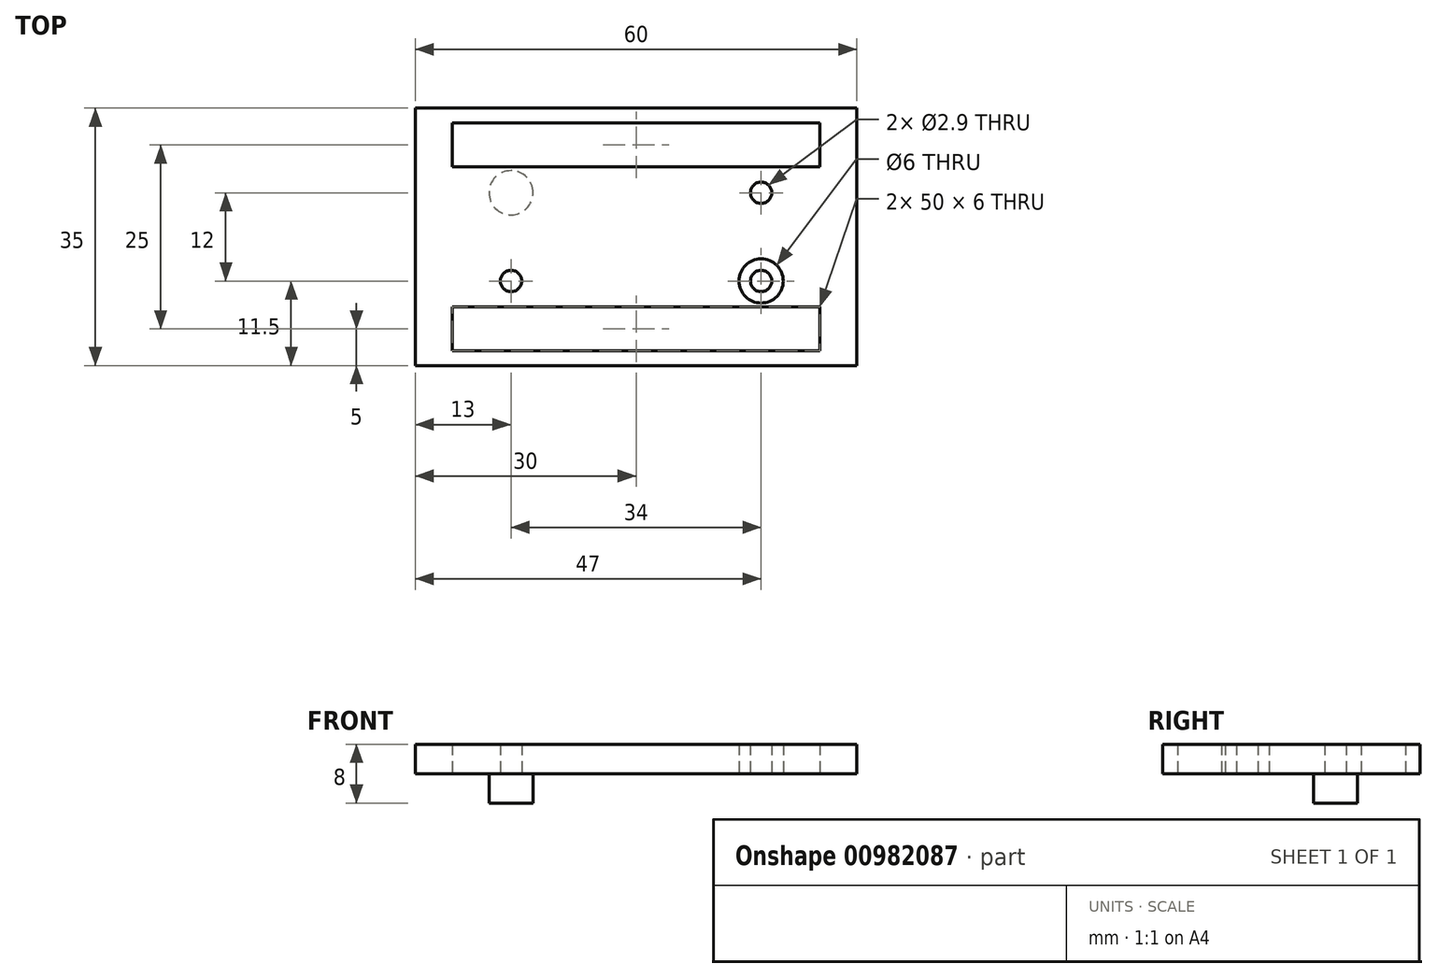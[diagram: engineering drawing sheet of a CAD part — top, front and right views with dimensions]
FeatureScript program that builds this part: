
annotation { "Feature Type Name" : "Feature", "Feature Type Description" : "" }
export const myFeature = defineFeature(function(context is Context, id is Id, definition is map)
    precondition{}
    {
        {
            var Q0;
            Q0=qCreatedBy(makeId("Top.planeOp"),FACE);
            var sketch = newSketch(context, id + "F0", { "sketchPlane" : qUnion([Q0])});
            skLineSegment(sketch, "E0.bottom", {"start": v(-30, 17.5) * mm, "end": v(30, 17.5) * mm});
            skLineSegment(sketch, "E0.top", {"start": v(-30, -17.5) * mm, "end": v(30, -17.5) * mm});
            skLineSegment(sketch, "E0.left", {"start": v(-30, 17.5) * mm, "end": v(-30, -17.5) * mm});
            skLineSegment(sketch, "E0.right", {"start": v(30, 17.5) * mm, "end": v(30, -17.5) * mm});
            skPoint(sketch, "E0.middle", {"position": v(0, 0) * mm});
            skLineSegment(sketch, "E1", {"start": v(-30, 17.5) * mm, "end": v(-30, 12.5) * mm, "construction": true});
            skLineSegment(sketch, "E2", {"start": v(-30, 12.5) * mm, "end": v(-25, 12.5) * mm, "construction": true});
            skLineSegment(sketch, "E3", {"start": v(30, 17.5) * mm, "end": v(30, 12.5) * mm, "construction": true});
            skLineSegment(sketch, "E4", {"start": v(30, 12.5) * mm, "end": v(25, 12.5) * mm, "construction": true});
            skLineSegment(sketch, "E5.bottom", {"start": v(-25, 12.5) * mm, "end": v(25, 12.5) * mm});
            skLineSegment(sketch, "E5.top", {"start": v(-25, 15.5) * mm, "end": v(25, 15.5) * mm});
            skLineSegment(sketch, "E5.left", {"start": v(-25, 12.5) * mm, "end": v(-25, 15.5) * mm});
            skLineSegment(sketch, "E5.right", {"start": v(25, 12.5) * mm, "end": v(25, 15.5) * mm});
            skLineSegment(sketch, "E6.MirrorCS", {"start": v(-25, 9.5) * mm, "end": v(25, 9.5) * mm});
            skLineSegment(sketch, "E7.MirrorCS", {"start": v(-25, 12.5) * mm, "end": v(-25, 9.5) * mm});
            skLineSegment(sketch, "E8.MirrorCS", {"start": v(25, 12.5) * mm, "end": v(25, 9.5) * mm});
            skLineSegment(sketch, "E9.MirrorCS", {"start": v(-25, -9.5) * mm, "end": v(25, -9.5) * mm});
            skLineSegment(sketch, "E10.MirrorCS", {"start": v(-25, -15.5) * mm, "end": v(25, -15.5) * mm});
            skLineSegment(sketch, "E11.MirrorCS", {"start": v(-25, -12.5) * mm, "end": v(-25, -15.5) * mm});
            skLineSegment(sketch, "E12.MirrorCS", {"start": v(-25, -12.5) * mm, "end": v(-25, -9.5) * mm});
            skLineSegment(sketch, "E13.MirrorCS", {"start": v(25, -12.5) * mm, "end": v(25, -9.5) * mm});
            skLineSegment(sketch, "E14.MirrorCS", {"start": v(25, -12.5) * mm, "end": v(25, -15.5) * mm});
            skLineSegment(sketch, "E15.bottom", {"start": v(25, 12.5) * mm, "end": v(-25, 12.5) * mm});
            skLineSegment(sketch, "E15.top", {"start": v(25, 14.1) * mm, "end": v(-25, 14.1) * mm});
            skLineSegment(sketch, "E15.left", {"start": v(25, 12.5) * mm, "end": v(25, 14.1) * mm});
            skLineSegment(sketch, "E15.right", {"start": v(-25, 12.5) * mm, "end": v(-25, 14.1) * mm});
            skLineSegment(sketch, "E16.MirrorCS", {"start": v(25, 10.9) * mm, "end": v(-25, 10.9) * mm});
            skLineSegment(sketch, "E17.MirrorCS", {"start": v(25, -10.9) * mm, "end": v(-25, -10.9) * mm});
            skLineSegment(sketch, "E18.MirrorCS", {"start": v(25, -14.1) * mm, "end": v(-25, -14.1) * mm});
            skLineSegment(sketch, "E19", {"start": v(-21.28, 14.1) * mm, "end": v(-21.28, 10.9) * mm, "construction": true});
            skLineSegment(sketch, "E20", {"start": v(-7.7, -10.9) * mm, "end": v(-7.7, -14.1) * mm, "construction": true});
            skSolve(sketch);
        }
        {
            var Q0;
            Q0=makeQuery(id+"F0.imprint","IMPRINT",FACE,{"disambiguationData":[TD([[makeQuery(id+"F0.imprint","IMPRINT",EDGE,{"derivedFrom":sQuery(id+"F0.wireOp",EDGE,"E0.bottom")}),-1.0]])]});
            extrude(context, id + "F1", {"entities" : qUnion([Q0]), "depth" : 8 * mm, "offsetDistance" : 25 * mm});
        }
        {
            var Q0;
            Q0=makeQuery(id+"F0.imprint","IMPRINT",FACE,{"disambiguationData":[TD([[makeQuery(id+"F0.imprint","IMPRINT",EDGE,{"derivedFrom":sQuery(id+"F0.wireOp",EDGE,"E5.top")}),-1.0]])]});
            var Q1;
            {var subQ0=sQuery(id+"F0.wireOp",EDGE,"E6.MirrorCS");Q1=makeQuery(id+"F0.imprint","IMPRINT",FACE,{"disambiguationData":[TD([[makeQuery(id+"F0.imprint","IMPRINT",EDGE,{"derivedFrom":subQ0}),1.0]])]});}
            var Q2;
            {var subQ0=sQuery(id+"F0.wireOp",EDGE,"E9.MirrorCS");Q2=makeQuery(id+"F0.imprint","IMPRINT",FACE,{"disambiguationData":[TD([[makeQuery(id+"F0.imprint","IMPRINT",EDGE,{"derivedFrom":subQ0}),-1.0]])]});}
            var Q3;
            {var subQ0=sQuery(id+"F0.wireOp",EDGE,"E10.MirrorCS");Q3=makeQuery(id+"F0.imprint","IMPRINT",FACE,{"disambiguationData":[TD([[makeQuery(id+"F0.imprint","IMPRINT",EDGE,{"derivedFrom":subQ0}),1.0]])]});}
            extrude(context, id + "F2", {"entities" : qUnion([Q0, Q1, Q2, Q3]), "operationType" : NewBodyOperationType.ADD, "depth" : 3 * mm, "offsetDistance" : 25 * mm});
        }
        {
            var Q0;
            {var subQ0=sQuery(id+"F0.wireOp",EDGE,"E14.MirrorCS");var subQ1=sQuery(id+"F0.wireOp",EDGE,"E11.MirrorCS");var subQ2=sQuery(id+"F0.wireOp",EDGE,"E10.MirrorCS");var subQ3=sQuery(id+"F0.wireOp",EDGE,"E13.MirrorCS");var subQ4=sQuery(id+"F0.wireOp",EDGE,"E12.MirrorCS");var subQ5=sQuery(id+"F0.wireOp",EDGE,"E9.MirrorCS");var subQ6=sQuery(id+"F0.wireOp",EDGE,"E8.MirrorCS");var subQ7=sQuery(id+"F0.wireOp",EDGE,"E7.MirrorCS");var subQ8=sQuery(id+"F0.wireOp",EDGE,"E6.MirrorCS");var subQ9=sQuery(id+"F0.wireOp",EDGE,"E5.right");var subQ10=sQuery(id+"F0.wireOp",EDGE,"E5.left");var subQ11=sQuery(id+"F0.wireOp",EDGE,"E5.top");Q0=makeQuery(id+"F2.boolean.opBoolean","MERGE",FACE,{"derivedFrom":[makeQuery(id+"F1.opExtrude","CAP_FACE",FACE,{"disambiguationData":[OSD([sQuery(id+"F0.wireOp",EDGE,"E0.bottom"),sQuery(id+"F0.wireOp",EDGE,"E0.top"),sQuery(id+"F0.wireOp",EDGE,"E0.left"),sQuery(id+"F0.wireOp",EDGE,"E0.right"),subQ11,subQ10,subQ9,subQ8,subQ7,subQ6,subQ5,subQ2,subQ1,subQ4,subQ3,subQ0,sQuery(id+"F0.wireOp",EDGE,"E15.left"),sQuery(id+"F0.wireOp",EDGE,"E15.right")])],"isStart":true}),makeQuery(id+"F2.opExtrude","CAP_FACE",FACE,{"disambiguationData":[OSD([subQ11,subQ10,subQ9,sQuery(id+"F0.wireOp",EDGE,"E15.top")])],"isStart":true}),makeQuery(id+"F2.opExtrude","CAP_FACE",FACE,{"disambiguationData":[OSD([subQ8,subQ7,subQ6,sQuery(id+"F0.wireOp",EDGE,"E16.MirrorCS")])],"isStart":true}),makeQuery(id+"F2.opExtrude","CAP_FACE",FACE,{"disambiguationData":[OSD([subQ5,subQ4,subQ3,sQuery(id+"F0.wireOp",EDGE,"E17.MirrorCS")])],"isStart":true}),makeQuery(id+"F2.opExtrude","CAP_FACE",FACE,{"disambiguationData":[OSD([subQ2,subQ1,subQ0,sQuery(id+"F0.wireOp",EDGE,"E18.MirrorCS")])],"isStart":true})]});}
            var sketch = newSketch(context, id + "F3", { "sketchPlane" : qUnion([Q0])});
            skLineSegment(sketch, "E21.bottom", {"start": v(17, -6) * mm, "end": v(-17, -6) * mm});
            skLineSegment(sketch, "E21.top", {"start": v(17, 6) * mm, "end": v(-17, 6) * mm});
            skLineSegment(sketch, "E21.left", {"start": v(17, -6) * mm, "end": v(17, 6) * mm});
            skLineSegment(sketch, "E21.right", {"start": v(-17, -6) * mm, "end": v(-17, 6) * mm});
            skPoint(sketch, "E21.middle", {"position": v(0, 0) * mm});
            skCircle(sketch, "E22", {"center": v(-17, 6) * mm, "radius": 3 * mm});
            skCircle(sketch, "E23", {"center": v(-17, 6) * mm, "radius": 1.45 * mm});
            skCircle(sketch, "E24.MirrorC", {"center": v(17, 6) * mm, "radius": 1.45 * mm});
            skCircle(sketch, "E25.MirrorC", {"center": v(17, 6) * mm, "radius": 3 * mm});
            skCircle(sketch, "E26.MirrorC", {"center": v(-17, -6) * mm, "radius": 3 * mm});
            skCircle(sketch, "E27.MirrorC", {"center": v(-17, -6) * mm, "radius": 1.45 * mm});
            skCircle(sketch, "E28.MirrorC", {"center": v(17, -6) * mm, "radius": 3 * mm});
            skCircle(sketch, "E29.MirrorC", {"center": v(17, -6) * mm, "radius": 1.45 * mm});
            skLineSegment(sketch, "E30.MirrorCS", {"start": v(-17, 6) * mm, "end": v(-17, -6) * mm});
            skLineSegment(sketch, "E31.MirrorCS", {"start": v(17, 6) * mm, "end": v(17, -6) * mm});
            skSolve(sketch);
        }
        {
            var Q0;
            {var subQ0=sQuery(id+"F3.wireOp",EDGE,"E30.MirrorCS");var subQ1=sQuery(id+"F3.wireOp",EDGE,"E22");var subQ2=makeQuery(id+"F3.imprint","INTERSECT",VERTEX,{"derivedFrom":[subQ1,subQ0]});Q0=makeQuery(id+"F3.imprint","IMPRINT",FACE,{"disambiguationData":[TD([[makeQuery(id+"F3.imprint","IMPRINT",EDGE,{"disambiguationData":[TD([[subQ2,1.0]])],"derivedFrom":subQ1}),1.0]])]});}
            var Q1;
            {var subQ0=sQuery(id+"F3.wireOp",EDGE,"E30.MirrorCS");var subQ1=sQuery(id+"F3.wireOp",EDGE,"E22");var subQ2=makeQuery(id+"F3.imprint","INTERSECT",VERTEX,{"derivedFrom":[subQ1,subQ0]});Q1=makeQuery(id+"F3.imprint","IMPRINT",FACE,{"disambiguationData":[TD([[makeQuery(id+"F3.imprint","IMPRINT",EDGE,{"disambiguationData":[TD([[subQ2,-1.0]])],"derivedFrom":subQ1}),1.0]])]});}
            var Q2;
            {var subQ0=sQuery(id+"F3.wireOp",EDGE,"E21.bottom");var subQ1=sQuery(id+"F3.wireOp",EDGE,"E26.MirrorC");var subQ2=makeQuery(id+"F3.imprint","INTERSECT",VERTEX,{"derivedFrom":[subQ1,subQ0]});Q2=makeQuery(id+"F3.imprint","IMPRINT",FACE,{"disambiguationData":[TD([[makeQuery(id+"F3.imprint","IMPRINT",EDGE,{"disambiguationData":[TD([[subQ2,-1.0]])],"derivedFrom":subQ1}),-1.0]])]});}
            var Q3;
            {var subQ0=sQuery(id+"F3.wireOp",EDGE,"E21.bottom");var subQ1=sQuery(id+"F3.wireOp",EDGE,"E26.MirrorC");var subQ2=makeQuery(id+"F3.imprint","INTERSECT",VERTEX,{"derivedFrom":[subQ1,subQ0]});Q3=makeQuery(id+"F3.imprint","IMPRINT",FACE,{"disambiguationData":[TD([[makeQuery(id+"F3.imprint","IMPRINT",EDGE,{"disambiguationData":[TD([[subQ2,1.0]])],"derivedFrom":subQ1}),-1.0]])]});}
            var Q4;
            {var subQ0=sQuery(id+"F3.wireOp",EDGE,"E21.top");var subQ1=sQuery(id+"F3.wireOp",EDGE,"E24.MirrorC");var subQ2=makeQuery(id+"F3.imprint","INTERSECT",VERTEX,{"derivedFrom":[subQ1,subQ0]});Q4=makeQuery(id+"F3.imprint","IMPRINT",FACE,{"disambiguationData":[TD([[makeQuery(id+"F3.imprint","IMPRINT",EDGE,{"disambiguationData":[TD([[subQ2,1.0]])],"derivedFrom":subQ1}),1.0]])]});}
            var Q5;
            {var subQ0=sQuery(id+"F3.wireOp",EDGE,"E21.top");var subQ1=sQuery(id+"F3.wireOp",EDGE,"E24.MirrorC");var subQ2=makeQuery(id+"F3.imprint","INTERSECT",VERTEX,{"derivedFrom":[subQ1,subQ0]});Q5=makeQuery(id+"F3.imprint","IMPRINT",FACE,{"disambiguationData":[TD([[makeQuery(id+"F3.imprint","IMPRINT",EDGE,{"disambiguationData":[TD([[subQ2,-1.0]])],"derivedFrom":subQ1}),1.0]])]});}
            var Q6;
            {var subQ0=sQuery(id+"F3.wireOp",EDGE,"E21.bottom");var subQ1=sQuery(id+"F3.wireOp",EDGE,"E28.MirrorC");var subQ2=makeQuery(id+"F3.imprint","INTERSECT",VERTEX,{"derivedFrom":[subQ1,subQ0]});Q6=makeQuery(id+"F3.imprint","IMPRINT",FACE,{"disambiguationData":[TD([[makeQuery(id+"F3.imprint","IMPRINT",EDGE,{"disambiguationData":[TD([[subQ2,1.0]])],"derivedFrom":subQ1}),1.0]])]});}
            var Q7;
            {var subQ0=sQuery(id+"F3.wireOp",EDGE,"E21.bottom");var subQ1=sQuery(id+"F3.wireOp",EDGE,"E28.MirrorC");var subQ2=makeQuery(id+"F3.imprint","INTERSECT",VERTEX,{"derivedFrom":[subQ1,subQ0]});Q7=makeQuery(id+"F3.imprint","IMPRINT",FACE,{"disambiguationData":[TD([[makeQuery(id+"F3.imprint","IMPRINT",EDGE,{"disambiguationData":[TD([[subQ2,-1.0]])],"derivedFrom":subQ1}),1.0]])]});}
            extrude(context, id + "F4", {"entities" : qUnion([Q0, Q1, Q2, Q3, Q4, Q5, Q6, Q7]), "operationType" : NewBodyOperationType.REMOVE, "oppositeDirection" : true, "depth" : 4 * mm, "offsetDistance" : 25 * mm});
        }
        {
            var Q0;
            {var subQ0=sQuery(id+"F0.wireOp",EDGE,"E14.MirrorCS");var subQ1=sQuery(id+"F0.wireOp",EDGE,"E11.MirrorCS");var subQ2=sQuery(id+"F0.wireOp",EDGE,"E10.MirrorCS");var subQ3=sQuery(id+"F0.wireOp",EDGE,"E13.MirrorCS");var subQ4=sQuery(id+"F0.wireOp",EDGE,"E12.MirrorCS");var subQ5=sQuery(id+"F0.wireOp",EDGE,"E9.MirrorCS");var subQ6=sQuery(id+"F0.wireOp",EDGE,"E8.MirrorCS");var subQ7=sQuery(id+"F0.wireOp",EDGE,"E7.MirrorCS");var subQ8=sQuery(id+"F0.wireOp",EDGE,"E6.MirrorCS");var subQ9=sQuery(id+"F0.wireOp",EDGE,"E5.right");var subQ10=sQuery(id+"F0.wireOp",EDGE,"E5.left");var subQ11=sQuery(id+"F0.wireOp",EDGE,"E5.top");Q0=makeQuery(id+"F4.boolean.opBoolean","SPLIT",FACE,{"disambiguationData":[TD([makeQuery(id+"F4.opExtrude","SWEPT_FACE",FACE,{"disambiguationData":[OSD([sQuery(id+"F3.wireOp",EDGE,"E27.MirrorC")])]})])],"derivedFrom":makeQuery(id+"F2.boolean.opBoolean","MERGE",FACE,{"derivedFrom":[makeQuery(id+"F1.opExtrude","CAP_FACE",FACE,{"disambiguationData":[OSD([sQuery(id+"F0.wireOp",EDGE,"E0.bottom"),sQuery(id+"F0.wireOp",EDGE,"E0.top"),sQuery(id+"F0.wireOp",EDGE,"E0.left"),sQuery(id+"F0.wireOp",EDGE,"E0.right"),subQ11,subQ10,subQ9,subQ8,subQ7,subQ6,subQ5,subQ2,subQ1,subQ4,subQ3,subQ0,sQuery(id+"F0.wireOp",EDGE,"E15.left"),sQuery(id+"F0.wireOp",EDGE,"E15.right")])],"isStart":true}),makeQuery(id+"F2.opExtrude","CAP_FACE",FACE,{"disambiguationData":[OSD([subQ11,subQ10,subQ9,sQuery(id+"F0.wireOp",EDGE,"E15.top")])],"isStart":true}),makeQuery(id+"F2.opExtrude","CAP_FACE",FACE,{"disambiguationData":[OSD([subQ8,subQ7,subQ6,sQuery(id+"F0.wireOp",EDGE,"E16.MirrorCS")])],"isStart":true}),makeQuery(id+"F2.opExtrude","CAP_FACE",FACE,{"disambiguationData":[OSD([subQ5,subQ4,subQ3,sQuery(id+"F0.wireOp",EDGE,"E17.MirrorCS")])],"isStart":true}),makeQuery(id+"F2.opExtrude","CAP_FACE",FACE,{"disambiguationData":[OSD([subQ2,subQ1,subQ0,sQuery(id+"F0.wireOp",EDGE,"E18.MirrorCS")])],"isStart":true})]})});}
            var Q1;
            {var subQ0=sQuery(id+"F0.wireOp",EDGE,"E14.MirrorCS");var subQ1=sQuery(id+"F0.wireOp",EDGE,"E11.MirrorCS");var subQ2=sQuery(id+"F0.wireOp",EDGE,"E10.MirrorCS");var subQ3=sQuery(id+"F0.wireOp",EDGE,"E13.MirrorCS");var subQ4=sQuery(id+"F0.wireOp",EDGE,"E12.MirrorCS");var subQ5=sQuery(id+"F0.wireOp",EDGE,"E9.MirrorCS");var subQ6=sQuery(id+"F0.wireOp",EDGE,"E8.MirrorCS");var subQ7=sQuery(id+"F0.wireOp",EDGE,"E7.MirrorCS");var subQ8=sQuery(id+"F0.wireOp",EDGE,"E6.MirrorCS");var subQ9=sQuery(id+"F0.wireOp",EDGE,"E5.right");var subQ10=sQuery(id+"F0.wireOp",EDGE,"E5.left");var subQ11=sQuery(id+"F0.wireOp",EDGE,"E5.top");Q1=makeQuery(id+"F4.boolean.opBoolean","SPLIT",FACE,{"disambiguationData":[TD([makeQuery(id+"F4.opExtrude","SWEPT_FACE",FACE,{"disambiguationData":[OSD([sQuery(id+"F3.wireOp",EDGE,"E29.MirrorC")])]})])],"derivedFrom":makeQuery(id+"F2.boolean.opBoolean","MERGE",FACE,{"derivedFrom":[makeQuery(id+"F1.opExtrude","CAP_FACE",FACE,{"disambiguationData":[OSD([sQuery(id+"F0.wireOp",EDGE,"E0.bottom"),sQuery(id+"F0.wireOp",EDGE,"E0.top"),sQuery(id+"F0.wireOp",EDGE,"E0.left"),sQuery(id+"F0.wireOp",EDGE,"E0.right"),subQ11,subQ10,subQ9,subQ8,subQ7,subQ6,subQ5,subQ2,subQ1,subQ4,subQ3,subQ0,sQuery(id+"F0.wireOp",EDGE,"E15.left"),sQuery(id+"F0.wireOp",EDGE,"E15.right")])],"isStart":true}),makeQuery(id+"F2.opExtrude","CAP_FACE",FACE,{"disambiguationData":[OSD([subQ11,subQ10,subQ9,sQuery(id+"F0.wireOp",EDGE,"E15.top")])],"isStart":true}),makeQuery(id+"F2.opExtrude","CAP_FACE",FACE,{"disambiguationData":[OSD([subQ8,subQ7,subQ6,sQuery(id+"F0.wireOp",EDGE,"E16.MirrorCS")])],"isStart":true}),makeQuery(id+"F2.opExtrude","CAP_FACE",FACE,{"disambiguationData":[OSD([subQ5,subQ4,subQ3,sQuery(id+"F0.wireOp",EDGE,"E17.MirrorCS")])],"isStart":true}),makeQuery(id+"F2.opExtrude","CAP_FACE",FACE,{"disambiguationData":[OSD([subQ2,subQ1,subQ0,sQuery(id+"F0.wireOp",EDGE,"E18.MirrorCS")])],"isStart":true})]})});}
            var Q2;
            {var subQ0=sQuery(id+"F0.wireOp",EDGE,"E14.MirrorCS");var subQ1=sQuery(id+"F0.wireOp",EDGE,"E11.MirrorCS");var subQ2=sQuery(id+"F0.wireOp",EDGE,"E10.MirrorCS");var subQ3=sQuery(id+"F0.wireOp",EDGE,"E13.MirrorCS");var subQ4=sQuery(id+"F0.wireOp",EDGE,"E12.MirrorCS");var subQ5=sQuery(id+"F0.wireOp",EDGE,"E9.MirrorCS");var subQ6=sQuery(id+"F0.wireOp",EDGE,"E8.MirrorCS");var subQ7=sQuery(id+"F0.wireOp",EDGE,"E7.MirrorCS");var subQ8=sQuery(id+"F0.wireOp",EDGE,"E6.MirrorCS");var subQ9=sQuery(id+"F0.wireOp",EDGE,"E5.right");var subQ10=sQuery(id+"F0.wireOp",EDGE,"E5.left");var subQ11=sQuery(id+"F0.wireOp",EDGE,"E5.top");Q2=makeQuery(id+"F4.boolean.opBoolean","SPLIT",FACE,{"disambiguationData":[TD([makeQuery(id+"F4.opExtrude","SWEPT_FACE",FACE,{"disambiguationData":[OSD([sQuery(id+"F3.wireOp",EDGE,"E24.MirrorC")])]})])],"derivedFrom":makeQuery(id+"F2.boolean.opBoolean","MERGE",FACE,{"derivedFrom":[makeQuery(id+"F1.opExtrude","CAP_FACE",FACE,{"disambiguationData":[OSD([sQuery(id+"F0.wireOp",EDGE,"E0.bottom"),sQuery(id+"F0.wireOp",EDGE,"E0.top"),sQuery(id+"F0.wireOp",EDGE,"E0.left"),sQuery(id+"F0.wireOp",EDGE,"E0.right"),subQ11,subQ10,subQ9,subQ8,subQ7,subQ6,subQ5,subQ2,subQ1,subQ4,subQ3,subQ0,sQuery(id+"F0.wireOp",EDGE,"E15.left"),sQuery(id+"F0.wireOp",EDGE,"E15.right")])],"isStart":true}),makeQuery(id+"F2.opExtrude","CAP_FACE",FACE,{"disambiguationData":[OSD([subQ11,subQ10,subQ9,sQuery(id+"F0.wireOp",EDGE,"E15.top")])],"isStart":true}),makeQuery(id+"F2.opExtrude","CAP_FACE",FACE,{"disambiguationData":[OSD([subQ8,subQ7,subQ6,sQuery(id+"F0.wireOp",EDGE,"E16.MirrorCS")])],"isStart":true}),makeQuery(id+"F2.opExtrude","CAP_FACE",FACE,{"disambiguationData":[OSD([subQ5,subQ4,subQ3,sQuery(id+"F0.wireOp",EDGE,"E17.MirrorCS")])],"isStart":true}),makeQuery(id+"F2.opExtrude","CAP_FACE",FACE,{"disambiguationData":[OSD([subQ2,subQ1,subQ0,sQuery(id+"F0.wireOp",EDGE,"E18.MirrorCS")])],"isStart":true})]})});}
            var Q3;
            {var subQ0=sQuery(id+"F0.wireOp",EDGE,"E14.MirrorCS");var subQ1=sQuery(id+"F0.wireOp",EDGE,"E11.MirrorCS");var subQ2=sQuery(id+"F0.wireOp",EDGE,"E10.MirrorCS");var subQ3=sQuery(id+"F0.wireOp",EDGE,"E13.MirrorCS");var subQ4=sQuery(id+"F0.wireOp",EDGE,"E12.MirrorCS");var subQ5=sQuery(id+"F0.wireOp",EDGE,"E9.MirrorCS");var subQ6=sQuery(id+"F0.wireOp",EDGE,"E8.MirrorCS");var subQ7=sQuery(id+"F0.wireOp",EDGE,"E7.MirrorCS");var subQ8=sQuery(id+"F0.wireOp",EDGE,"E6.MirrorCS");var subQ9=sQuery(id+"F0.wireOp",EDGE,"E5.right");var subQ10=sQuery(id+"F0.wireOp",EDGE,"E5.left");var subQ11=sQuery(id+"F0.wireOp",EDGE,"E5.top");Q3=makeQuery(id+"F4.boolean.opBoolean","SPLIT",FACE,{"disambiguationData":[TD([makeQuery(id+"F4.opExtrude","SWEPT_FACE",FACE,{"disambiguationData":[OSD([sQuery(id+"F3.wireOp",EDGE,"E23")])]})])],"derivedFrom":makeQuery(id+"F2.boolean.opBoolean","MERGE",FACE,{"derivedFrom":[makeQuery(id+"F1.opExtrude","CAP_FACE",FACE,{"disambiguationData":[OSD([sQuery(id+"F0.wireOp",EDGE,"E0.bottom"),sQuery(id+"F0.wireOp",EDGE,"E0.top"),sQuery(id+"F0.wireOp",EDGE,"E0.left"),sQuery(id+"F0.wireOp",EDGE,"E0.right"),subQ11,subQ10,subQ9,subQ8,subQ7,subQ6,subQ5,subQ2,subQ1,subQ4,subQ3,subQ0,sQuery(id+"F0.wireOp",EDGE,"E15.left"),sQuery(id+"F0.wireOp",EDGE,"E15.right")])],"isStart":true}),makeQuery(id+"F2.opExtrude","CAP_FACE",FACE,{"disambiguationData":[OSD([subQ11,subQ10,subQ9,sQuery(id+"F0.wireOp",EDGE,"E15.top")])],"isStart":true}),makeQuery(id+"F2.opExtrude","CAP_FACE",FACE,{"disambiguationData":[OSD([subQ8,subQ7,subQ6,sQuery(id+"F0.wireOp",EDGE,"E16.MirrorCS")])],"isStart":true}),makeQuery(id+"F2.opExtrude","CAP_FACE",FACE,{"disambiguationData":[OSD([subQ5,subQ4,subQ3,sQuery(id+"F0.wireOp",EDGE,"E17.MirrorCS")])],"isStart":true}),makeQuery(id+"F2.opExtrude","CAP_FACE",FACE,{"disambiguationData":[OSD([subQ2,subQ1,subQ0,sQuery(id+"F0.wireOp",EDGE,"E18.MirrorCS")])],"isStart":true})]})});}
            extrude(context, id + "F5", {"entities" : qUnion([Q0, Q1, Q2, Q3]), "operationType" : NewBodyOperationType.REMOVE, "oppositeDirection" : true, "depth" : 25 * mm, "offsetDistance" : 25 * mm});
        }
    });
